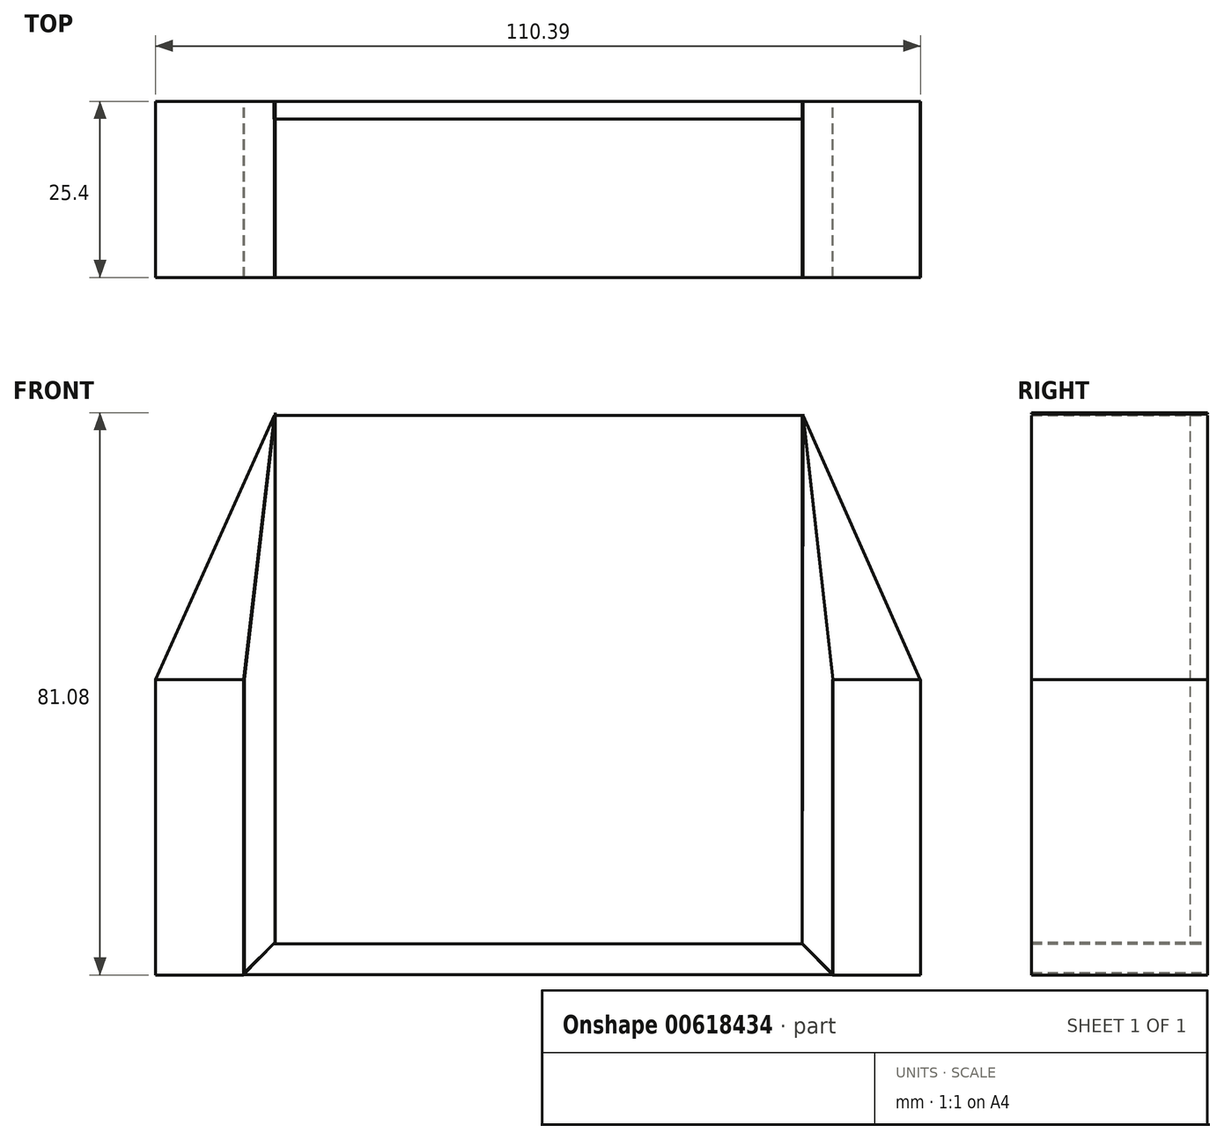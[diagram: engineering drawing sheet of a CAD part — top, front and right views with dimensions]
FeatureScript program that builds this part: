
annotation { "Feature Type Name" : "Feature", "Feature Type Description" : "" }
export const myFeature = defineFeature(function(context is Context, id is Id, definition is map)
    precondition{}
    {
        {
            var Q0;
            Q0=qCreatedBy(makeId("Front.planeOp"),FACE);
            var sketch = newSketch(context, id + "F0", { "sketchPlane" : qUnion([Q0])});
            skLineSegment(sketch, "E0.bottom", {"start": v(-38.1, 38.1) * mm, "end": v(38.1, 38.1) * mm});
            skLineSegment(sketch, "E0.top", {"start": v(-38.1, -38.1) * mm, "end": v(38.1, -38.1) * mm});
            skLineSegment(sketch, "E0.left", {"start": v(-38.1, 38.1) * mm, "end": v(-38.1, -38.1) * mm});
            skLineSegment(sketch, "E0.right", {"start": v(38.1, 38.1) * mm, "end": v(38.1, -38.1) * mm});
            skPoint(sketch, "E0.middle", {"position": v(0, 0) * mm});
            skSolve(sketch);
        }
        {
            var Q0;
            Q0=qCreatedBy(makeId("Front.planeOp"),FACE);
            var sketch = newSketch(context, id + "F1", { "sketchPlane" : qUnion([Q0])});
            skLineSegment(sketch, "E1.bottom", {"start": v(-42.49, 0) * mm, "end": v(-55.19, 0) * mm});
            skLineSegment(sketch, "E1.top", {"start": v(-42.49, -42.6) * mm, "end": v(-55.19, -42.6) * mm});
            skLineSegment(sketch, "E1.left", {"start": v(-42.49, 0) * mm, "end": v(-42.49, -42.6) * mm});
            skLineSegment(sketch, "E1.right", {"start": v(-55.19, 0) * mm, "end": v(-55.19, -42.6) * mm});
            skLineSegment(sketch, "E2.bottom", {"start": v(42.49, 0) * mm, "end": v(55.19, 0) * mm});
            skLineSegment(sketch, "E2.top", {"start": v(42.49, -42.6) * mm, "end": v(55.19, -42.6) * mm});
            skLineSegment(sketch, "E2.left", {"start": v(42.49, 0) * mm, "end": v(42.49, -42.6) * mm});
            skLineSegment(sketch, "E2.right", {"start": v(55.19, 0) * mm, "end": v(55.19, -42.6) * mm});
            skSolve(sketch);
        }
        {
            var Q0;
            Q0=makeQuery(id+"F0.imprint","IMPRINT",FACE,{"disambiguationData":[TD([[makeQuery(id+"F0.imprint","IMPRINT",EDGE,{"derivedFrom":sQuery(id+"F0.wireOp",EDGE,"E0.bottom")}),-1.0]])]});
            var sketch = newSketch(context, id + "F2", { "sketchPlane" : qUnion([Q0])});
            skPoint(sketch, "E3", {"position": v(-42.5, -42.56) * mm});
            skPoint(sketch, "E4", {"position": v(42.49, -42.56) * mm});
            skPoint(sketch, "E5", {"position": v(-38.1, -38.06) * mm});
            skPoint(sketch, "E6", {"position": v(38.1, -38.08) * mm});
            skLineSegment(sketch, "E7", {"start": v(-42.5, -42.56) * mm, "end": v(-38.1, -38.06) * mm});
            skLineSegment(sketch, "E8", {"start": v(-42.5, -42.56) * mm, "end": v(42.49, -42.56) * mm});
            skLineSegment(sketch, "E9", {"start": v(38.1, -38.08) * mm, "end": v(-38.1, -38.06) * mm});
            skLineSegment(sketch, "E10", {"start": v(42.49, -42.56) * mm, "end": v(38.1, -38.08) * mm});
            skSolve(sketch);
        }
        {
            var Q0;
            Q0=qCreatedBy(makeId("Front.planeOp"),FACE);
            var sketch = newSketch(context, id + "F3", { "sketchPlane" : qUnion([Q0])});
            skPoint(sketch, "E11", {"position": v(-42.36, 0) * mm});
            skPoint(sketch, "E12", {"position": v(-37.95, 38.5) * mm});
            skPoint(sketch, "E13", {"position": v(-37.95, -37.82) * mm});
            skPoint(sketch, "E14", {"position": v(-42.36, -42.23) * mm});
            skLineSegment(sketch, "E15", {"start": v(-42.36, 0) * mm, "end": v(-37.95, 38.5) * mm});
            skLineSegment(sketch, "E16", {"start": v(-37.95, -37.82) * mm, "end": v(-42.36, -42.23) * mm});
            skLineSegment(sketch, "E17", {"start": v(-42.36, 0) * mm, "end": v(-42.36, -42.23) * mm});
            skLineSegment(sketch, "E18", {"start": v(-37.95, -37.82) * mm, "end": v(-37.95, 38.5) * mm});
            skSolve(sketch);
        }
        {
            var Q0;
            Q0=qCreatedBy(makeId("Front.planeOp"),FACE);
            var sketch = newSketch(context, id + "F4", { "sketchPlane" : qUnion([Q0])});
            skPoint(sketch, "E19", {"position": v(38.18, 38.3) * mm});
            skPoint(sketch, "E20", {"position": v(42.54, 0) * mm});
            skPoint(sketch, "E21", {"position": v(42.54, -42.47) * mm});
            skPoint(sketch, "E22", {"position": v(38.1, -38.07) * mm});
            skLineSegment(sketch, "E23", {"start": v(38.18, 38.3) * mm, "end": v(42.54, 0) * mm});
            skLineSegment(sketch, "E24", {"start": v(42.54, -42.47) * mm, "end": v(38.1, -38.07) * mm});
            skLineSegment(sketch, "E25", {"start": v(38.18, 38.3) * mm, "end": v(38.1, -38.07) * mm});
            skLineSegment(sketch, "E26", {"start": v(42.54, -42.47) * mm, "end": v(42.54, 0) * mm});
            skSolve(sketch);
        }
        {
            var Q0;
            Q0=qCreatedBy(makeId("Front.planeOp"),FACE);
            var sketch = newSketch(context, id + "F5", { "sketchPlane" : qUnion([Q0])});
            skLineSegment(sketch, "E27", {"start": v(55.13, 0) * mm, "end": v(38.18, 38.13) * mm});
            skLineSegment(sketch, "E28", {"start": v(38.18, 38.13) * mm, "end": v(42.52, 0) * mm});
            skLineSegment(sketch, "E29", {"start": v(42.52, 0) * mm, "end": v(55.13, 0) * mm});
            skLineSegment(sketch, "E30", {"start": v(-55.2, 0) * mm, "end": v(-42.48, 0) * mm});
            skLineSegment(sketch, "E31", {"start": v(-42.48, 0) * mm, "end": v(-38.09, 38.13) * mm});
            skLineSegment(sketch, "E32", {"start": v(-38.09, 38.13) * mm, "end": v(-55.2, 0) * mm});
            skSolve(sketch);
        }
        {
            var Q0;
            Q0=makeQuery(id+"F5.imprint","IMPRINT",FACE,{"disambiguationData":[TD([[makeQuery(id+"F5.imprint","IMPRINT",EDGE,{"derivedFrom":sQuery(id+"F5.wireOp",EDGE,"E30")}),1.0]])]});
            var Q1;
            Q1=makeQuery(id+"F3.imprint","IMPRINT",FACE,{"disambiguationData":[TD([[makeQuery(id+"F3.imprint","IMPRINT",EDGE,{"derivedFrom":sQuery(id+"F3.wireOp",EDGE,"E15")}),-1.0]])]});
            var Q2;
            Q2=makeQuery(id+"F1.imprint","IMPRINT",FACE,{"disambiguationData":[TD([[makeQuery(id+"F1.imprint","IMPRINT",EDGE,{"derivedFrom":sQuery(id+"F1.wireOp",EDGE,"E1.bottom")}),1.0]])]});
            var Q3;
            {var subQ4=sQuery(id+"F2.wireOp",EDGE,"E8");Q3=makeQuery(id+"F2.imprint","IMPRINT",FACE,{"disambiguationData":[TD([[makeQuery(id+"F2.imprint","IMPRINT",EDGE,{"derivedFrom":subQ4}),1.0]])]});}
            var Q4;
            Q4=makeQuery(id+"F1.imprint","IMPRINT",FACE,{"disambiguationData":[TD([[makeQuery(id+"F1.imprint","IMPRINT",EDGE,{"derivedFrom":sQuery(id+"F1.wireOp",EDGE,"E2.bottom")}),-1.0]])]});
            var Q5;
            Q5=makeQuery(id+"F4.imprint","IMPRINT",FACE,{"disambiguationData":[TD([[makeQuery(id+"F4.imprint","IMPRINT",EDGE,{"derivedFrom":sQuery(id+"F4.wireOp",EDGE,"E23")}),-1.0]])]});
            var Q6;
            Q6=makeQuery(id+"F5.imprint","IMPRINT",FACE,{"disambiguationData":[TD([[makeQuery(id+"F5.imprint","IMPRINT",EDGE,{"derivedFrom":sQuery(id+"F5.wireOp",EDGE,"E27")}),1.0]])]});
            extrude(context, id + "F6", {"entities" : qUnion([Q0, Q1, Q2, Q3, Q4, Q5, Q6]), "depth" : 25.4 * mm, "offsetDistance" : 25.4 * mm});
        }
        {
            var Q0;
            Q0=makeQuery(id+"F0.imprint","IMPRINT",FACE,{"disambiguationData":[TD([[makeQuery(id+"F0.imprint","IMPRINT",EDGE,{"derivedFrom":sQuery(id+"F0.wireOp",EDGE,"E0.bottom")}),-1.0]])]});
            extrude(context, id + "F7", {"entities" : qUnion([Q0]), "depth" : 2.54 * mm, "offsetDistance" : 25.4 * mm});
        }
    });
